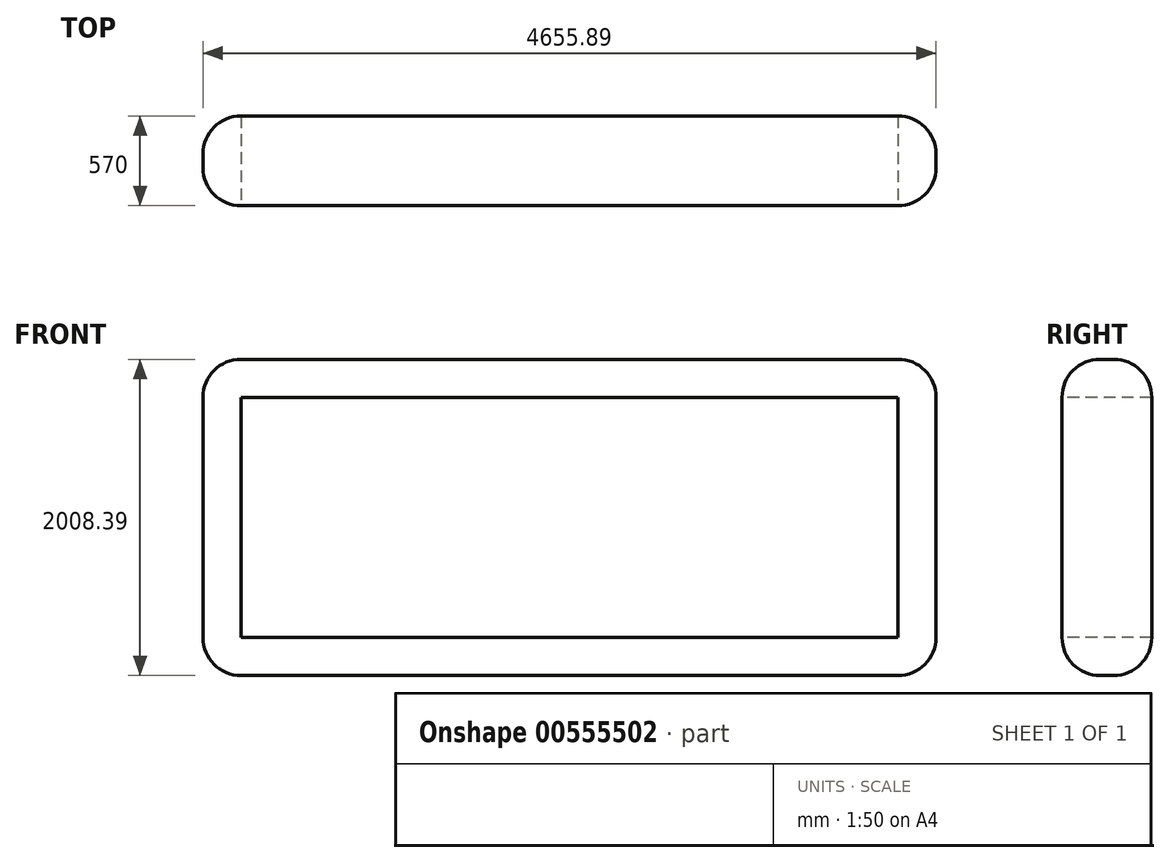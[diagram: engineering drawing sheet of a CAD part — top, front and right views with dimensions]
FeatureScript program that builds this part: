
annotation { "Feature Type Name" : "Feature", "Feature Type Description" : "" }
export const myFeature = defineFeature(function(context is Context, id is Id, definition is map)
    precondition{}
    {
        {
            var Q0;
            Q0=qCreatedBy(makeId("Front.planeOp"),FACE);
            var sketch = newSketch(context, id + "F0", { "sketchPlane" : qUnion([Q0])});
            skLineSegment(sketch, "E0.bottom", {"start": v(-2060.8, 1390.06) * mm, "end": v(2595.09, 1390.06) * mm});
            skLineSegment(sketch, "E0.top", {"start": v(-2060.8, -618.33) * mm, "end": v(2595.09, -618.33) * mm});
            skLineSegment(sketch, "E0.left", {"start": v(-2060.8, 1390.06) * mm, "end": v(-2060.8, -618.33) * mm});
            skLineSegment(sketch, "E0.right", {"start": v(2595.09, 1390.06) * mm, "end": v(2595.09, -618.33) * mm});
            skSolve(sketch);
        }
        {
            var Q0;
            Q0 = qSketchRegion(id + "F0", true);
            extrude(context, id + "F1", {"entities" : qUnion([Q0]), "depth" : 570 * mm, "offsetDistance" : 25 * mm});
        }
        {
            var Q0;
            Q0=makeQuery(id+"F1.opExtrude","CAP_EDGE",EDGE,{"disambiguationData":[OSD([sQuery(id+"F0.wireOp",EDGE,"E0.bottom")])],"isStart":false});
            var Q1;
            Q1=makeQuery(id+"F1.opExtrude","CAP_EDGE",EDGE,{"disambiguationData":[OSD([sQuery(id+"F0.wireOp",EDGE,"E0.top")])],"isStart":false});
            var Q2;
            Q2=makeQuery(id+"F1.opExtrude","CAP_EDGE",EDGE,{"disambiguationData":[OSD([sQuery(id+"F0.wireOp",EDGE,"E0.left")])],"isStart":false});
            var Q3;
            Q3=makeQuery(id+"F1.opExtrude","CAP_EDGE",EDGE,{"disambiguationData":[OSD([sQuery(id+"F0.wireOp",EDGE,"E0.right")])],"isStart":false});
            var Q4;
            Q4=makeQuery(id+"F1.opExtrude","SWEPT_EDGE",EDGE,{"disambiguationData":[OSD([sQuery(id+"F0.wireOp",EDGE,"E0.bottom"),sQuery(id+"F0.wireOp",EDGE,"E0.right")])]});
            var Q5;
            Q5=makeQuery(id+"F1.opExtrude","CAP_EDGE",EDGE,{"disambiguationData":[OSD([sQuery(id+"F0.wireOp",EDGE,"E0.bottom")])],"isStart":true});
            var Q6;
            Q6=makeQuery(id+"F1.opExtrude","CAP_EDGE",EDGE,{"disambiguationData":[OSD([sQuery(id+"F0.wireOp",EDGE,"E0.left")])],"isStart":true});
            var Q7;
            Q7=makeQuery(id+"F1.opExtrude","CAP_EDGE",EDGE,{"disambiguationData":[OSD([sQuery(id+"F0.wireOp",EDGE,"E0.right")])],"isStart":true});
            var Q8;
            Q8=makeQuery(id+"F1.opExtrude","CAP_EDGE",EDGE,{"disambiguationData":[OSD([sQuery(id+"F0.wireOp",EDGE,"E0.top")])],"isStart":true});
            var Q9;
            Q9=makeQuery(id+"F1.opExtrude","SWEPT_EDGE",EDGE,{"disambiguationData":[OSD([sQuery(id+"F0.wireOp",EDGE,"E0.top"),sQuery(id+"F0.wireOp",EDGE,"E0.right")])]});
            var Q10;
            Q10=makeQuery(id+"F1.opExtrude","SWEPT_EDGE",EDGE,{"disambiguationData":[OSD([sQuery(id+"F0.wireOp",EDGE,"E0.bottom"),sQuery(id+"F0.wireOp",EDGE,"E0.left")])]});
            var Q11;
            Q11=makeQuery(id+"F1.opExtrude","SWEPT_EDGE",EDGE,{"disambiguationData":[OSD([sQuery(id+"F0.wireOp",EDGE,"E0.top"),sQuery(id+"F0.wireOp",EDGE,"E0.left")])]});
            fillet(context, id + "F2", {"entities" : qUnion([Q0, Q1, Q2, Q3, Q4, Q5, Q6, Q7, Q8, Q9, Q10, Q11]), "radius" : 241.42 * mm, "tangentPropagation" : true, "allowEdgeOverflow" : false});
        }
        {
            var Q0;
            Q0=makeQuery(id+"F1.opExtrude","CAP_FACE",FACE,{"disambiguationData":[OSD([sQuery(id+"F0.wireOp",EDGE,"E0.bottom"),sQuery(id+"F0.wireOp",EDGE,"E0.top"),sQuery(id+"F0.wireOp",EDGE,"E0.left"),sQuery(id+"F0.wireOp",EDGE,"E0.right")])],"isStart":false});
            var sketch = newSketch(context, id + "F3", { "sketchPlane" : qUnion([Q0])});
            skLineSegment(sketch, "E1", {"start": v(-728.3, 767.6) * mm, "end": v(1309, 767.6) * mm});
            skLineSegment(sketch, "E2", {"start": v(1309, 767.6) * mm, "end": v(1309, -29.6) * mm});
            skLineSegment(sketch, "E3", {"start": v(1309, -29.6) * mm, "end": v(-736.75, -29.6) * mm});
            skLineSegment(sketch, "E4", {"start": v(-736.75, -29.6) * mm, "end": v(-736.75, 767.6) * mm});
            skSolve(sketch);
        }
        {
            var Q0;
            Q0 = qSketchRegion(id + "F3", true);
            var Q1;
            {var subQ0=sQuery(id+"F0.wireOp",EDGE,"E0.right");var subQ1=sQuery(id+"F0.wireOp",EDGE,"E0.left");var subQ2=sQuery(id+"F0.wireOp",EDGE,"E0.top");var subQ3=sQuery(id+"F0.wireOp",EDGE,"E0.bottom");var subQ4=makeQuery(id+"F1.opExtrude","CAP_FACE",FACE,{"disambiguationData":[OSD([subQ3,subQ2,subQ1,subQ0])],"isStart":false});Q1=makeQuery(id+"F3.imprint","IMPRINT",FACE,{"disambiguationData":[TD([[makeQuery(id+"F3.imprint","IMPRINT",EDGE,{"derivedFrom":makeQuery(id+"F2.opFillet","BLEND_EDGE",EDGE,{"blendedFrom":[makeQuery(id+"F1.opExtrude","CAP_EDGE",EDGE,{"disambiguationData":[OSD([subQ3])],"isStart":false}),subQ4],"blendedInto":[subQ4]})}),1.0]])]});}
            extrude(context, id + "F4", {"entities" : qUnion([Q0, Q1]), "operationType" : NewBodyOperationType.REMOVE, "oppositeDirection" : true, "depth" : 1630 * mm, "offsetDistance" : 25 * mm});
        }
    });
